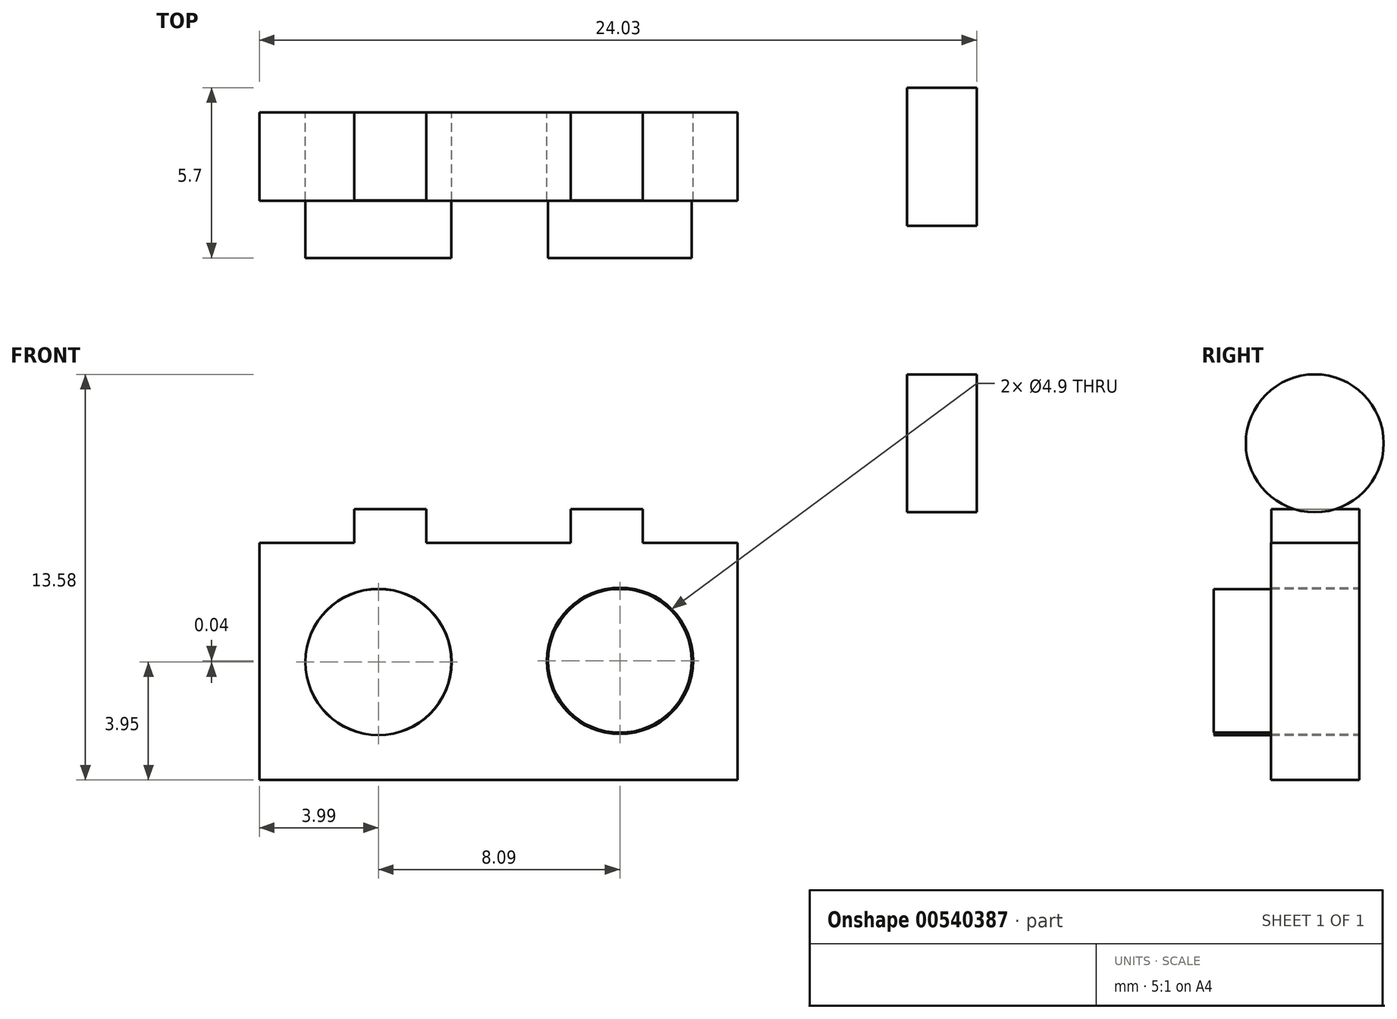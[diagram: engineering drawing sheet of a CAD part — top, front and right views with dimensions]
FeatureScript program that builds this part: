
annotation { "Feature Type Name" : "Feature", "Feature Type Description" : "" }
export const myFeature = defineFeature(function(context is Context, id is Id, definition is map)
    precondition{}
    {
        {
            var Q0;
            Q0=qCreatedBy(makeId("Front.planeOp"),FACE);
            var sketch = newSketch(context, id + "F0", { "sketchPlane" : qUnion([Q0])});
            skLineSegment(sketch, "E0", {"start": v(-8.01, 0) * mm, "end": v(-8.01, 7.94) * mm});
            skLineSegment(sketch, "E1", {"start": v(-8.01, 7.94) * mm, "end": v(-24.03, 7.94) * mm});
            skLineSegment(sketch, "E2", {"start": v(-24.03, 7.94) * mm, "end": v(-24.03, 0) * mm});
            skLineSegment(sketch, "E3", {"start": v(-24.03, 0) * mm, "end": v(-8.01, 0) * mm});
            skCircle(sketch, "E4", {"center": v(-20.04, 3.95) * mm, "radius": 2.45 * mm});
            skCircle(sketch, "E5", {"center": v(-11.95, 4) * mm, "radius": 2.45 * mm});
            skLineSegment(sketch, "E6", {"start": v(-20.85, 7.94) * mm, "end": v(-20.85, 9.07) * mm});
            skLineSegment(sketch, "E7", {"start": v(-20.85, 9.07) * mm, "end": v(-18.44, 9.07) * mm});
            skLineSegment(sketch, "E8", {"start": v(-18.44, 9.07) * mm, "end": v(-18.44, 7.94) * mm});
            skLineSegment(sketch, "E9", {"start": v(-18.44, 7.94) * mm, "end": v(-13.6, 7.94) * mm});
            skLineSegment(sketch, "E10", {"start": v(-13.6, 7.94) * mm, "end": v(-13.6, 9.07) * mm});
            skLineSegment(sketch, "E11", {"start": v(-13.6, 9.07) * mm, "end": v(-11.2, 9.07) * mm});
            skLineSegment(sketch, "E12", {"start": v(-11.2, 9.07) * mm, "end": v(-11.2, 7.94) * mm});
            skSolve(sketch);
        }
        {
            var Q0;
            {var subQ4=sQuery(id+"F0.wireOp",EDGE,"E0");Q0=makeQuery(id+"F0.imprint","IMPRINT",FACE,{"disambiguationData":[TD([[makeQuery(id+"F0.imprint","IMPRINT",EDGE,{"derivedFrom":subQ4}),1.0]])]});}
            extrude(context, id + "F1", {"entities" : qUnion([Q0]), "depth" : 2.96 * mm, "offsetDistance" : 25 * mm});
        }
        {
            var Q0;
            Q0=makeQuery(id+"F1.opExtrude","CAP_FACE",FACE,{"disambiguationData":[OSD([sQuery(id+"F0.wireOp",EDGE,"E0"),sQuery(id+"F0.wireOp",EDGE,"E1"),sQuery(id+"F0.wireOp",EDGE,"E2"),sQuery(id+"F0.wireOp",EDGE,"E3"),sQuery(id+"F0.wireOp",EDGE,"E4"),sQuery(id+"F0.wireOp",EDGE,"E5"),sQuery(id+"F0.wireOp",EDGE,"E9")])],"isStart":false});
            var sketch = newSketch(context, id + "F2", { "sketchPlane" : qUnion([Q0])});
            skCircle(sketch, "E13", {"center": v(-20.04, 3.95) * mm, "radius": 2.45 * mm});
            skCircle(sketch, "E14", {"center": v(-11.95, 4) * mm, "radius": 2.4 * mm});
            skSolve(sketch);
        }
        {
            var Q0;
            Q0=makeQuery(id+"F2.imprint","IMPRINT",FACE,{"disambiguationData":[TD([[makeQuery(id+"F2.imprint","IMPRINT",EDGE,{"derivedFrom":sQuery(id+"F2.wireOp",EDGE,"PouIKoqI-ImN8-zTDx-3qge-Od1ypUP8jgoV")}),1.0]])]});
            var Q1;
            Q1=makeQuery(id+"F2.imprint","IMPRINT",FACE,{"disambiguationData":[TD([[makeQuery(id+"F2.imprint","IMPRINT",EDGE,{"derivedFrom":sQuery(id+"F2.wireOp",EDGE,"E13")}),1.0]])]});
            extrude(context, id + "F3", {"entities" : qUnion([Q0, Q1]), "depth" : 1.92 * mm, "offsetDistance" : 25 * mm});
        }
        {
            var Q0;
            Q0=makeQuery(id+"F1.opExtrude","CAP_FACE",FACE,{"disambiguationData":[OSD([sQuery(id+"F0.wireOp",EDGE,"E0"),sQuery(id+"F0.wireOp",EDGE,"E1"),sQuery(id+"F0.wireOp",EDGE,"E2"),sQuery(id+"F0.wireOp",EDGE,"E3"),sQuery(id+"F0.wireOp",EDGE,"E4"),sQuery(id+"F0.wireOp",EDGE,"E5"),sQuery(id+"F0.wireOp",EDGE,"E9")])],"isStart":false});
            var sketch = newSketch(context, id + "F4", { "sketchPlane" : qUnion([Q0])});
            skCircle(sketch, "E15", {"center": v(-11.95, 4) * mm, "radius": 2.4 * mm});
            skSolve(sketch);
        }
        {
            var Q0;
            Q0=makeQuery(id+"F4.imprint","IMPRINT",FACE,{"disambiguationData":[TD([[makeQuery(id+"F4.imprint","IMPRINT",EDGE,{"derivedFrom":sQuery(id+"F4.wireOp",EDGE,"E15")}),1.0]])]});
            extrude(context, id + "F5", {"entities" : qUnion([Q0]), "depth" : 1.92 * mm, "offsetDistance" : 25 * mm});
        }
        {
            var Q0;
            {var subQ0=sQuery(id+"F0.wireOp",EDGE,"E6");Q0=makeQuery(id+"F0.imprint","IMPRINT",FACE,{"disambiguationData":[TD([[makeQuery(id+"F0.imprint","IMPRINT",EDGE,{"derivedFrom":subQ0}),-1.0]])]});}
            var Q1;
            {var subQ0=sQuery(id+"F0.wireOp",EDGE,"E10");Q1=makeQuery(id+"F0.imprint","IMPRINT",FACE,{"disambiguationData":[TD([[makeQuery(id+"F0.imprint","IMPRINT",EDGE,{"derivedFrom":subQ0}),-1.0]])]});}
            extrude(context, id + "F6", {"entities" : qUnion([Q0, Q1]), "operationType" : NewBodyOperationType.ADD, "depth" : 2.95 * mm, "offsetDistance" : 25 * mm});
        }
        {
            var Q0;
            Q0=qCreatedBy(makeId("Right.planeOp"),FACE);
            var sketch = newSketch(context, id + "F7", { "sketchPlane" : qUnion([Q0])});
            skCircle(sketch, "E16", {"center": v(-1.5, 11.27) * mm, "radius": 2.31 * mm});
            skSolve(sketch);
        }
        {
            var Q0;
            Q0=qSketchRegion(id+"F7",true);
            extrude(context, id + "F8", {"entities" : qUnion([Q0]), "oppositeDirection" : true, "depth" : 2.33 * mm, "offsetDistance" : 25 * mm});
        }
    });
